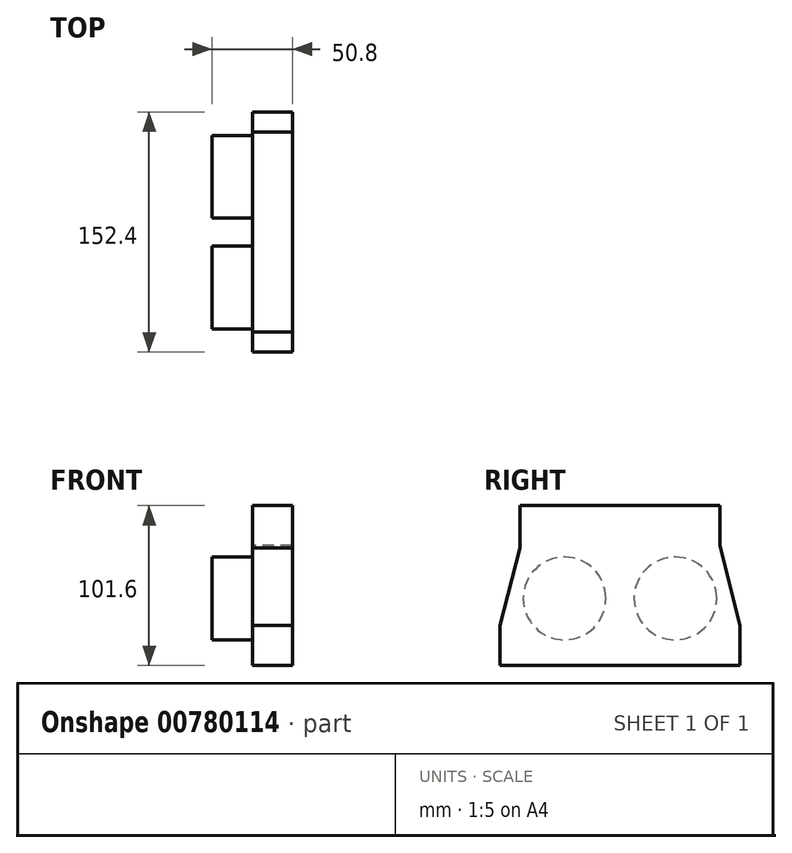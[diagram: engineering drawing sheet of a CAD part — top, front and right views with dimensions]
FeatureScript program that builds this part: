
annotation { "Feature Type Name" : "Feature", "Feature Type Description" : "" }
export const myFeature = defineFeature(function(context is Context, id is Id, definition is map)
    precondition{}
    {
        {
            var Q0;
            Q0=qCreatedBy(makeId("Right.planeOp"),FACE);
            var sketch = newSketch(context, id + "F0", { "sketchPlane" : qUnion([Q0])});
            skLineSegment(sketch, "E0.bottom", {"start": v(76.2, -42.57) * mm, "end": v(-76.2, -42.57) * mm});
            skLineSegment(sketch, "E0.top", {"start": v(76.2, -17.17) * mm, "end": v(-76.2, -17.17) * mm});
            skLineSegment(sketch, "E0.left", {"start": v(76.2, -42.57) * mm, "end": v(76.2, -17.17) * mm});
            skLineSegment(sketch, "E0.right", {"start": v(-76.2, -42.57) * mm, "end": v(-76.2, -17.17) * mm});
            skPoint(sketch, "E0.middle", {"position": v(0, -29.87) * mm});
            skLineSegment(sketch, "E1.bottom", {"start": v(-63.5, -17.17) * mm, "end": v(63.5, -17.17) * mm});
            skLineSegment(sketch, "E1.top", {"start": v(-63.5, 59.03) * mm, "end": v(63.5, 59.03) * mm});
            skLineSegment(sketch, "E1.left", {"start": v(-63.5, 32.02) * mm, "end": v(-63.5, 59.03) * mm});
            skLineSegment(sketch, "E1.right", {"start": v(63.5, 33.63) * mm, "end": v(63.5, 59.03) * mm});
            skLineSegment(sketch, "E2", {"start": v(-76.2, -17.17) * mm, "end": v(-63.5, 32.02) * mm});
            skLineSegment(sketch, "E3", {"start": v(76.2, -17.17) * mm, "end": v(63.5, 33.63) * mm});
            skSolve(sketch);
        }
        {
            var Q0;
            Q0 = qSketchRegion(id + "F0", true);
            extrude(context, id + "F1", {"entities" : qUnion([Q0]), "depth" : 25.4 * mm, "offsetDistance" : 25.4 * mm});
        }
        {
            var Q0;
            Q0=qCreatedBy(makeId("Right.planeOp"),FACE);
            var sketch = newSketch(context, id + "F2", { "sketchPlane" : qUnion([Q0])});
            skCircle(sketch, "E4", {"center": v(35.2, 0) * mm, "radius": 26.25 * mm});
            skCircle(sketch, "E5", {"center": v(-35.2, 0) * mm, "radius": 26.25 * mm});
            skSolve(sketch);
        }
        {
            var Q0;
            Q0 = qSketchRegion(id + "F2", true);
            extrude(context, id + "F3", {"entities" : qUnion([Q0]), "operationType" : NewBodyOperationType.ADD, "oppositeDirection" : true, "depth" : 25.4 * mm, "offsetDistance" : 25.4 * mm});
        }
    });
